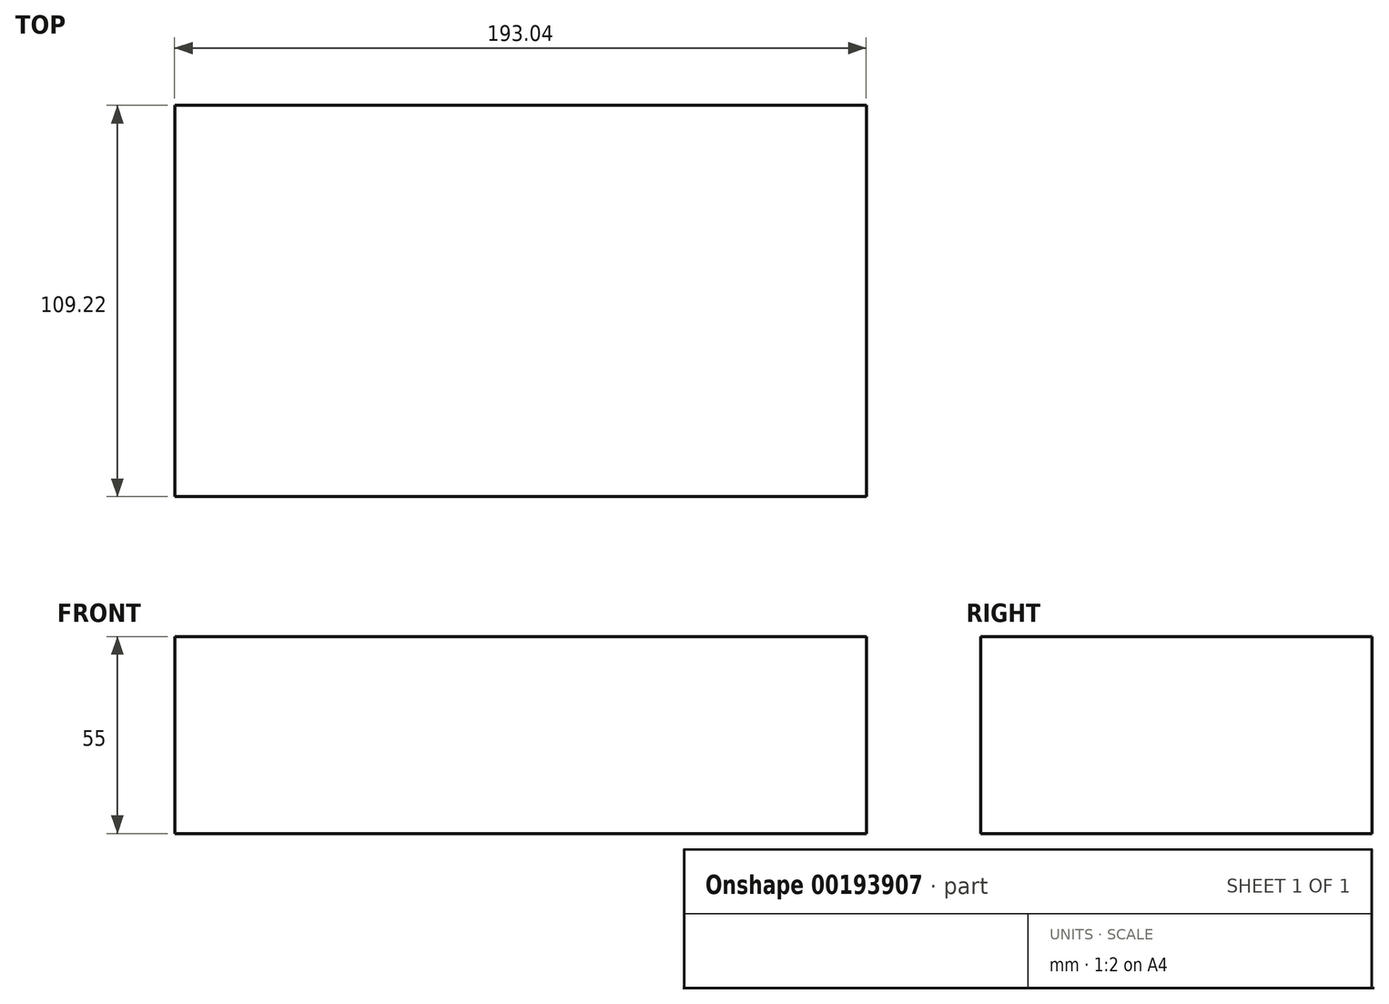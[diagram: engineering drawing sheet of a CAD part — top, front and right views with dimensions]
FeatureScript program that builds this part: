
annotation { "Feature Type Name" : "Feature", "Feature Type Description" : "" }
export const myFeature = defineFeature(function(context is Context, id is Id, definition is map)
    precondition{}
    {
        {
            var Q0;
            Q0=qCreatedBy(makeId("Top.planeOp"),FACE);
            var sketch = newSketch(context, id + "F0", { "sketchPlane" : qUnion([Q0])});
            skLineSegment(sketch, "E0.bottom", {"start": v(-105.63, 48.1) * mm, "end": v(87.41, 48.1) * mm});
            skLineSegment(sketch, "E0.top", {"start": v(-105.63, -61.12) * mm, "end": v(87.41, -61.12) * mm});
            skLineSegment(sketch, "E0.left", {"start": v(-105.63, 48.1) * mm, "end": v(-105.63, -61.12) * mm});
            skLineSegment(sketch, "E0.right", {"start": v(87.41, 48.1) * mm, "end": v(87.41, -61.12) * mm});
            skSolve(sketch);
        }
        {
            var Q0;
            Q0=makeQuery(id+"F0.imprint","IMPRINT",FACE,{"disambiguationData":[TD([[makeQuery(id+"F0.imprint","IMPRINT",EDGE,{"derivedFrom":sQuery(id+"F0.wireOp",EDGE,"E0.bottom")}),-1.0]])]});
            extrude(context, id + "F1", {"entities" : qUnion([Q0]), "depth" : 55 * mm});
        }
    });
